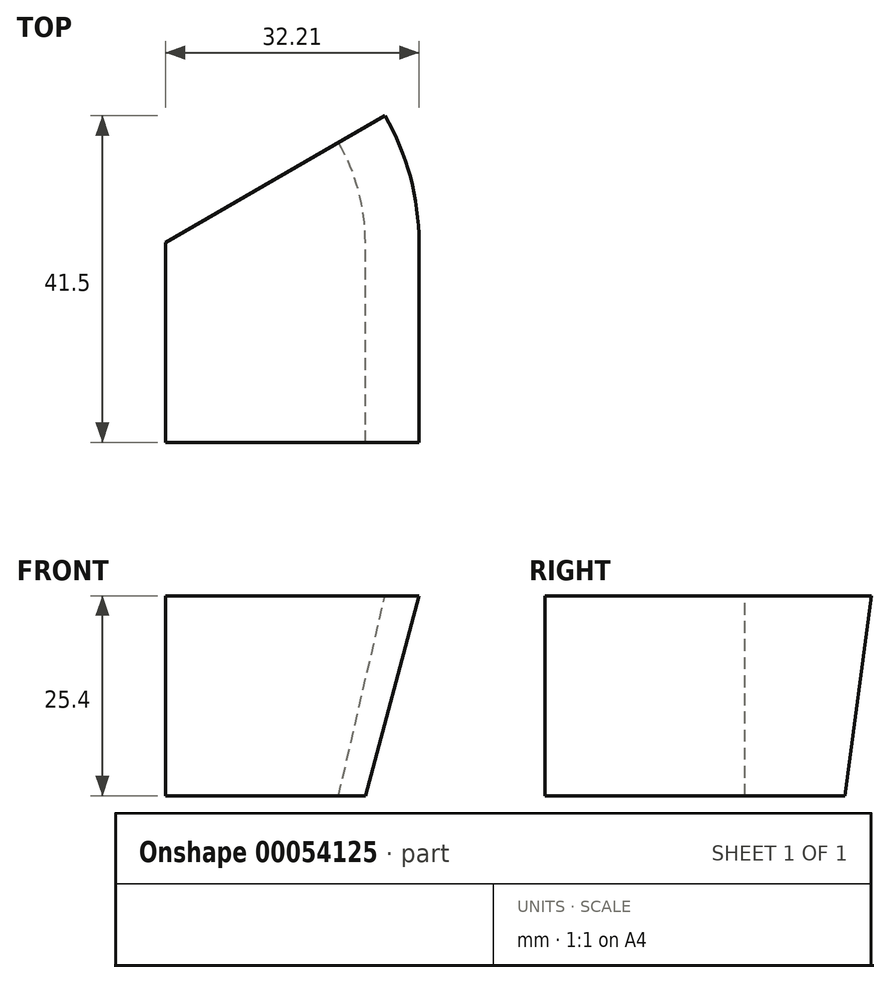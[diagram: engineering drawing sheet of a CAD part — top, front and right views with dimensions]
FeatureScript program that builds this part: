
annotation { "Feature Type Name" : "Feature", "Feature Type Description" : "" }
export const myFeature = defineFeature(function(context is Context, id is Id, definition is map)
    precondition{}
    {
        {
            var Q0;
            Q0=qCreatedBy(makeId("Front.planeOp"),FACE);
            var sketch = newSketch(context, id + "F0", { "sketchPlane" : qUnion([Q0])});
            skLineSegment(sketch, "E0.bottom", {"start": v(0, 0) * mm, "end": v(25.4, 0) * mm});
            skLineSegment(sketch, "E0.top", {"start": v(0, 25.4) * mm, "end": v(32.2, 25.4) * mm});
            skLineSegment(sketch, "E0.left", {"start": v(0, 0) * mm, "end": v(0, 25.4) * mm});
            skLineSegment(sketch, "E0.right", {"start": v(25.4, 0) * mm, "end": v(32.2, 25.4) * mm});
            skSolve(sketch);
        }
        {
            var Q0;
            Q0=makeQuery(id+"F0.imprint","IMPRINT",FACE,{"disambiguationData":[TD([[makeQuery(id+"F0.imprint","IMPRINT",EDGE,{"derivedFrom":sQuery(id+"F0.wireOp",EDGE,"E0.bottom")}),1.0]])]});
            extrude(context, id + "F1", {"entities" : qUnion([Q0]), "depth" : 25.4 * mm});
        }
        {
            var Q0;
            Q0 = qSketchRegion(id + "F0", true);
            var Q1;
            Q1=makeQuery(id+"F1.opExtrude","CAP_EDGE",EDGE,{"disambiguationData":[OSD([sQuery(id+"F0.wireOp",EDGE,"E0.left")])],"isStart":true});
            revolve(context, id + "F2", {"operationType" : NewBodyOperationType.ADD, "entities" : qUnion([Q0]), "axis" : qUnion([Q1]), "revolveType" : RevolveType.ONE_DIRECTION, "angle" : 30 * degree});
        }
    });
